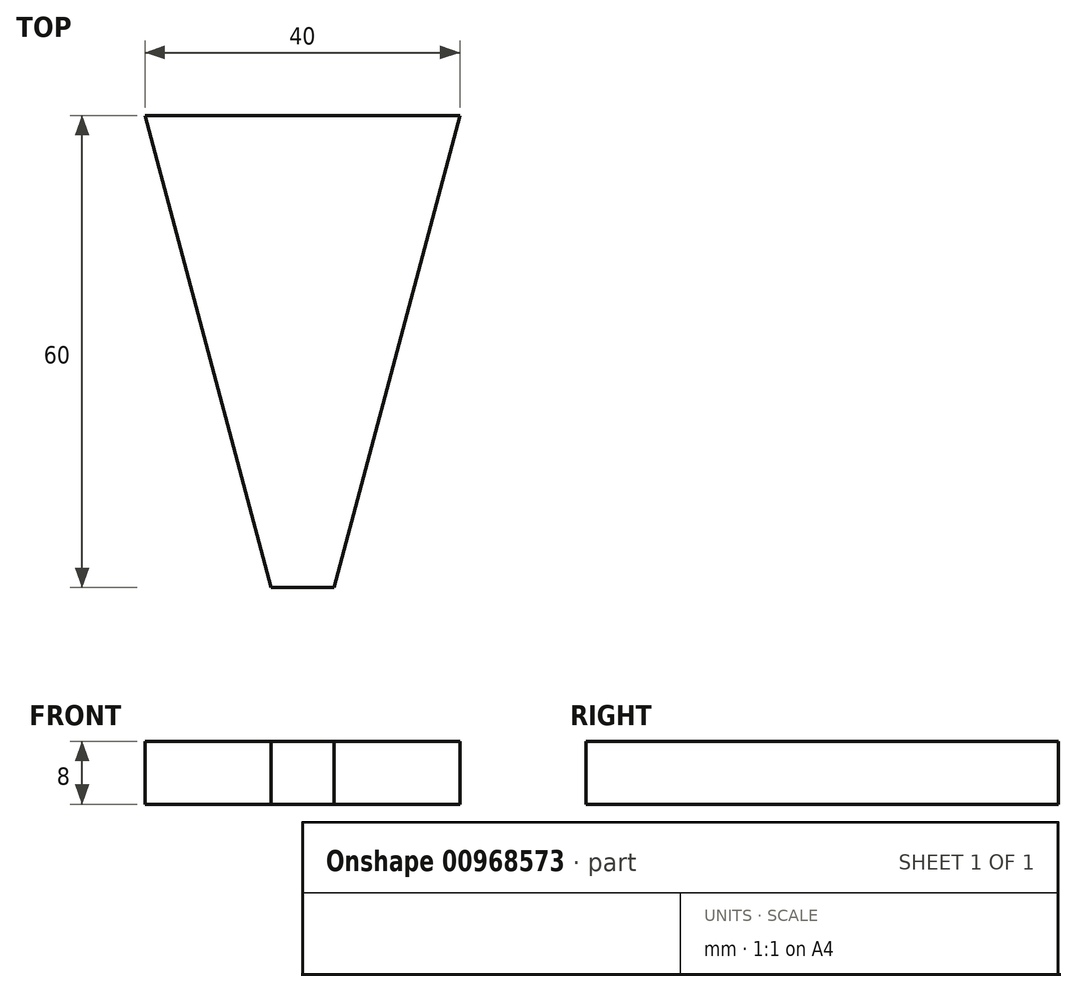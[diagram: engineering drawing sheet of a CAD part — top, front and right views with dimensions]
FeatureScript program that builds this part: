
annotation { "Feature Type Name" : "Feature", "Feature Type Description" : "" }
export const myFeature = defineFeature(function(context is Context, id is Id, definition is map)
    precondition{}
    {
        {
            var Q0;
            Q0=qCreatedBy(makeId("Top.planeOp"),FACE);
            var sketch = newSketch(context, id + "F0", { "sketchPlane" : qUnion([Q0])});
            skLineSegment(sketch, "E0", {"start": v(0, 0) * mm, "end": v(0, 60) * mm, "construction": true});
            skLineSegment(sketch, "E1", {"start": v(0, 60) * mm, "end": v(-20, 60) * mm});
            skLineSegment(sketch, "E2", {"start": v(-20, 60) * mm, "end": v(-4, 0) * mm});
            skLineSegment(sketch, "E3", {"start": v(-4, 0) * mm, "end": v(0, 0) * mm});
            skLineSegment(sketch, "E4.MirrorCS", {"start": v(0, 60) * mm, "end": v(20, 60) * mm});
            skLineSegment(sketch, "E5.MirrorCS", {"start": v(20, 60) * mm, "end": v(4, 0) * mm});
            skLineSegment(sketch, "E6.MirrorCS", {"start": v(4, 0) * mm, "end": v(0, 0) * mm});
            skSolve(sketch);
        }
        {
            var Q0;
            Q0 = qSketchRegion(id + "F0", true);
            extrude(context, id + "F1", {"entities" : qUnion([Q0]), "depth" : 8 * mm, "offsetDistance" : 25 * mm});
        }
    });
